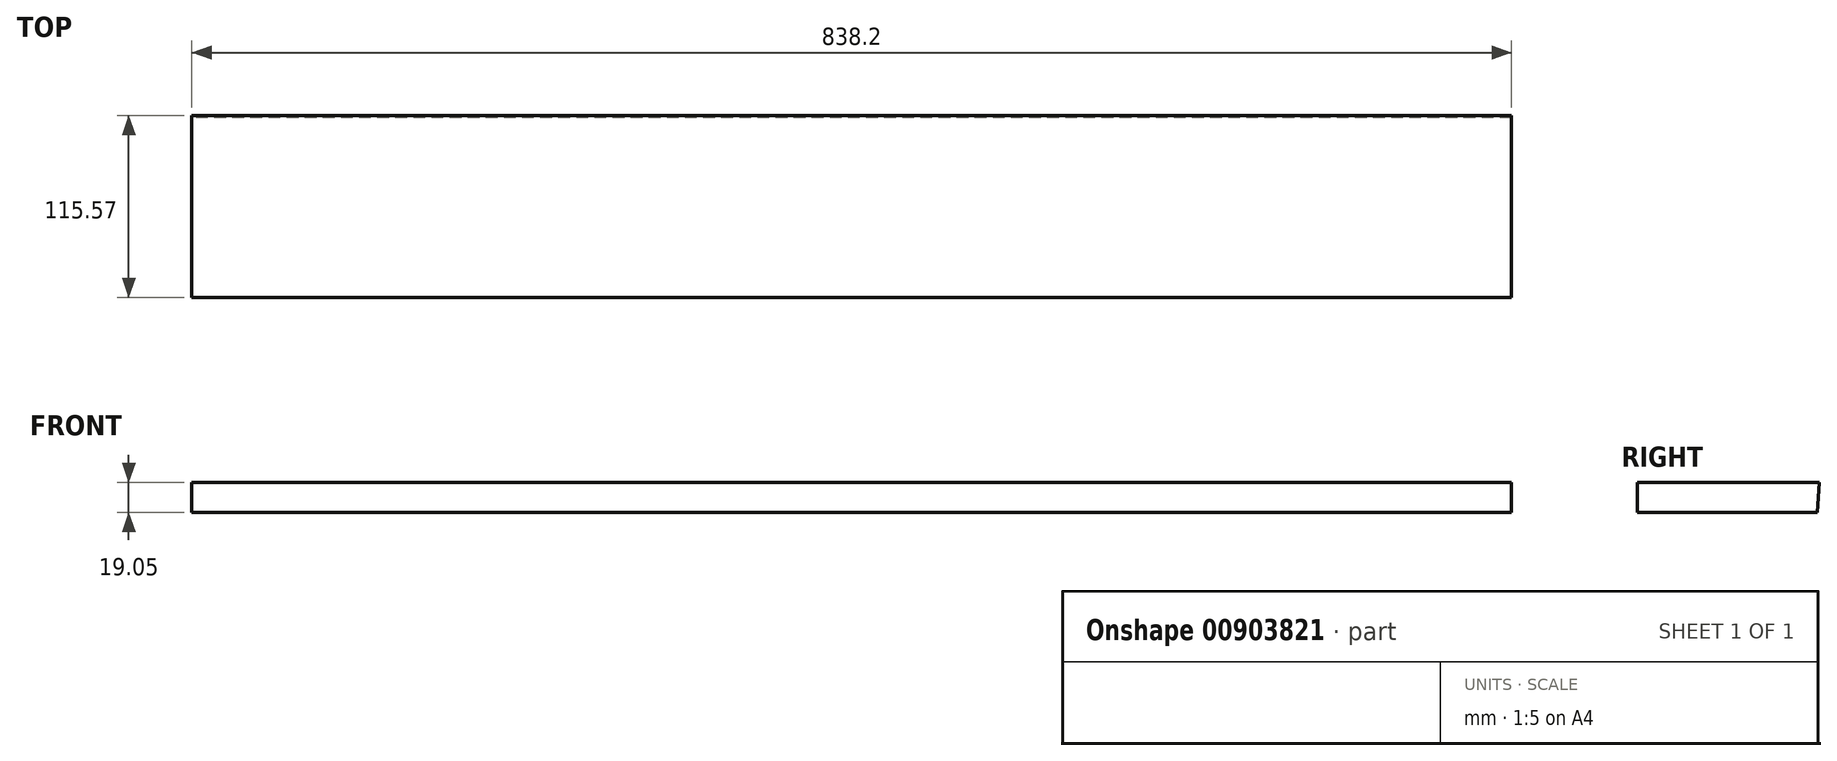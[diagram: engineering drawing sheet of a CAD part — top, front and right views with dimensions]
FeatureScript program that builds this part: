
annotation { "Feature Type Name" : "Feature", "Feature Type Description" : "" }
export const myFeature = defineFeature(function(context is Context, id is Id, definition is map)
    precondition{}
    {
        {
            var Q0;
            Q0=qCreatedBy(makeId("Top.planeOp"),FACE);
            var sketch = newSketch(context, id + "F0", { "sketchPlane" : qUnion([Q0])});
            skLineSegment(sketch, "E0.bottom", {"start": v(0, 0) * mm, "end": v(838.2, 0) * mm});
            skLineSegment(sketch, "E0.top", {"start": v(0, 115.57) * mm, "end": v(838.2, 115.57) * mm});
            skLineSegment(sketch, "E0.left", {"start": v(0, 0) * mm, "end": v(0, 115.57) * mm});
            skLineSegment(sketch, "E0.right", {"start": v(838.2, 0) * mm, "end": v(838.2, 115.57) * mm});
            skSolve(sketch);
        }
        {
            var Q0;
            Q0 = qSketchRegion(id + "F0", true);
            extrude(context, id + "F1", {"entities" : qUnion([Q0]), "depth" : 19.05 * mm, "offsetDistance" : 25.4 * mm});
        }
        {
            var Q0;
            Q0=makeQuery(id+"F1.opExtrude","SWEPT_FACE",FACE,{"disambiguationData":[OSD([sQuery(id+"F0.wireOp",EDGE,"E0.left")])]});
            var sketch = newSketch(context, id + "F2", { "sketchPlane" : qUnion([Q0])});
            skLineSegment(sketch, "E1", {"start": v(-115.57, 19.05) * mm, "end": v(-114.24, 0) * mm});
            skSolve(sketch);
        }
        {
            var Q0;
            Q0 = qSketchRegion(id + "F2", true);
            var Q1;
            {var subQ0=sQuery(id+"F2.wireOp",EDGE,"E1");Q1=makeQuery(id+"F2.imprint","IMPRINT",FACE,{"disambiguationData":[TD([[makeQuery(id+"F2.imprint","IMPRINT",EDGE,{"derivedFrom":subQ0}),-1.0]])]});}
            extrude(context, id + "F3", {"entities" : qUnion([Q0, Q1]), "operationType" : NewBodyOperationType.REMOVE, "endBound" : BoundingType.THROUGH_ALL, "oppositeDirection" : true, "depth" : 25.4 * mm, "offsetDistance" : 25.4 * mm});
        }
    });
